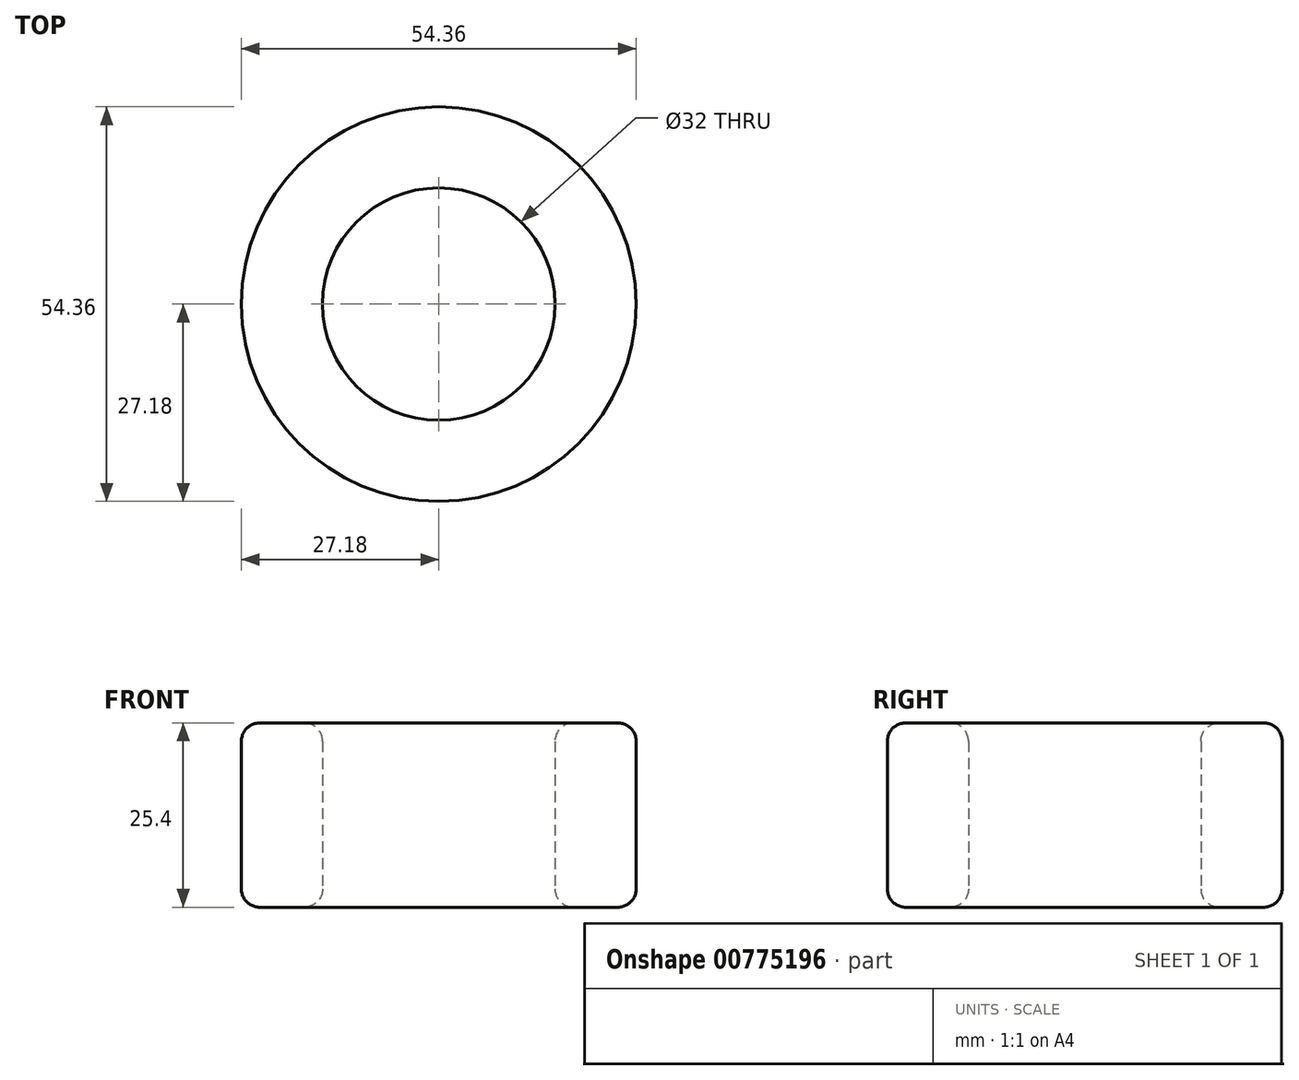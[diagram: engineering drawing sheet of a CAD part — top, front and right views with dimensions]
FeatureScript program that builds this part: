
annotation { "Feature Type Name" : "Feature", "Feature Type Description" : "" }
export const myFeature = defineFeature(function(context is Context, id is Id, definition is map)
    precondition{}
    {
        {
            var Q0;
            Q0=qCreatedBy(makeId("Top.planeOp"),FACE);
            var sketch = newSketch(context, id + "F0", { "sketchPlane" : qUnion([Q0])});
            skCircle(sketch, "E0", {"center": v(0, 0) * mm, "radius": 16 * mm});
            skCircle(sketch, "E1", {"center": v(0, 0) * mm, "radius": 27.18 * mm});
            skSolve(sketch);
        }
        {
            var Q0;
            Q0=makeQuery(id+"F0.imprint","IMPRINT",FACE,{"disambiguationData":[TD([[makeQuery(id+"F0.imprint","IMPRINT",EDGE,{"derivedFrom":sQuery(id+"F0.wireOp",EDGE,"E0")}),-1.0]])]});
            extrude(context, id + "F1", {"entities" : qUnion([Q0]), "depth" : 25.4 * mm, "offsetDistance" : 25.4 * mm});
        }
        {
            var Q0;
            Q0=makeQuery(id+"F1.opExtrude","CAP_EDGE",EDGE,{"disambiguationData":[OSD([sQuery(id+"F0.wireOp",EDGE,"E1")])],"isStart":true});
            fillet(context, id + "F2", {"entities" : qUnion([Q0]), "radius" : 2.54 * mm, "tangentPropagation" : true, "allowEdgeOverflow" : false});
        }
        {
            var Q0;
            Q0=makeQuery(id+"F1.opExtrude","CAP_EDGE",EDGE,{"disambiguationData":[OSD([sQuery(id+"F0.wireOp",EDGE,"E0")])],"isStart":true});
            var Q1;
            Q1=makeQuery(id+"F1.opExtrude","CAP_EDGE",EDGE,{"disambiguationData":[OSD([sQuery(id+"F0.wireOp",EDGE,"E1")])],"isStart":false});
            var Q2;
            Q2=makeQuery(id+"F1.opExtrude","CAP_EDGE",EDGE,{"disambiguationData":[OSD([sQuery(id+"F0.wireOp",EDGE,"E0")])],"isStart":false});
            fillet(context, id + "F3", {"entities" : qUnion([Q0, Q1, Q2]), "radius" : 2.54 * mm, "tangentPropagation" : true, "allowEdgeOverflow" : false});
        }
    });
